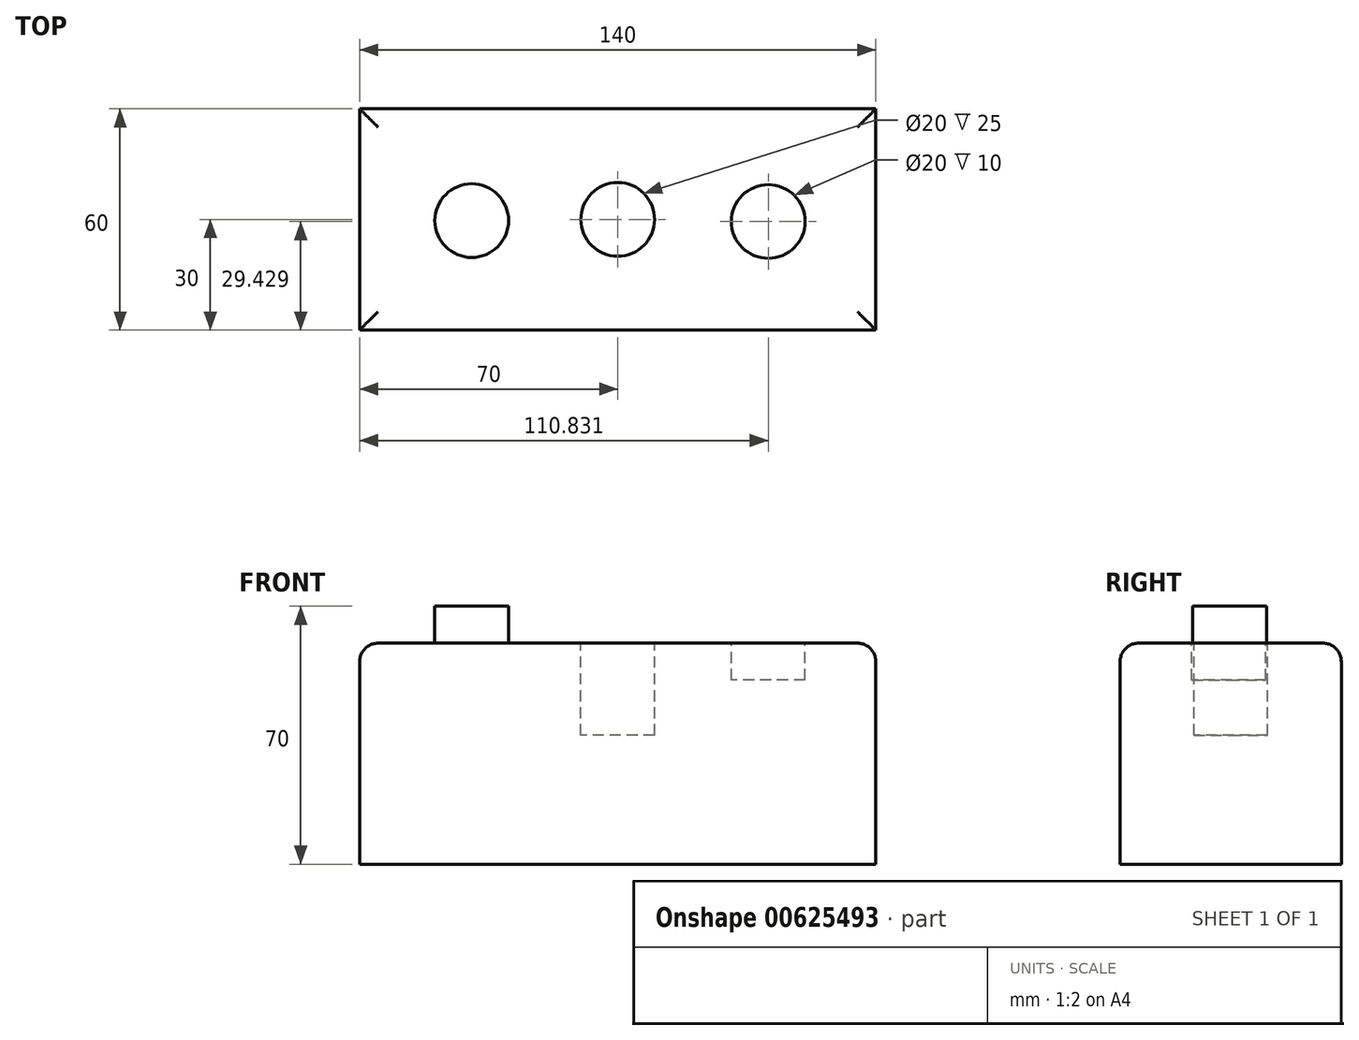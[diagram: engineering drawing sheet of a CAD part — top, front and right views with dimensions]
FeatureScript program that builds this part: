
annotation { "Feature Type Name" : "Feature", "Feature Type Description" : "" }
export const myFeature = defineFeature(function(context is Context, id is Id, definition is map)
    precondition{}
    {
        {
            var Q0;
            Q0=qCreatedBy(makeId("Top.planeOp"),FACE);
            var sketch = newSketch(context, id + "F0", { "sketchPlane" : qUnion([Q0])});
            skLineSegment(sketch, "E0.bottom", {"start": v(70, -30) * mm, "end": v(-70, -30) * mm});
            skLineSegment(sketch, "E0.top", {"start": v(70, 30) * mm, "end": v(-70, 30) * mm});
            skLineSegment(sketch, "E0.left", {"start": v(70, -30) * mm, "end": v(70, 30) * mm});
            skLineSegment(sketch, "E0.right", {"start": v(-70, -30) * mm, "end": v(-70, 30) * mm});
            skPoint(sketch, "E0.middle", {"position": v(0, 0) * mm});
            skSolve(sketch);
        }
        {
            var Q0;
            Q0 = qSketchRegion(id + "F0", true);
            extrude(context, id + "F1", {"entities" : qUnion([Q0]), "depth" : 60 * mm, "offsetDistance" : 25 * mm});
        }
        {
            var Q0;
            Q0=makeQuery(id+"F1.opExtrude","CAP_FACE",FACE,{"disambiguationData":[OSD([sQuery(id+"F0.wireOp",EDGE,"E0.bottom"),sQuery(id+"F0.wireOp",EDGE,"E0.top"),sQuery(id+"F0.wireOp",EDGE,"E0.left"),sQuery(id+"F0.wireOp",EDGE,"E0.right")])],"isStart":false});
            var sketch = newSketch(context, id + "F2", { "sketchPlane" : qUnion([Q0])});
            skLineSegment(sketch, "E1", {"start": v(-70, 0) * mm, "end": v(-50, 0) * mm});
            skSolve(sketch);
        }
        {
            var Q0;
            {var subQ1=makeQuery(id+"F1.opExtrude","CAP_EDGE",EDGE,{"disambiguationData":[OSD([sQuery(id+"F0.wireOp",EDGE,"E0.bottom")])],"isStart":false});Q0=makeQuery(id+"F2.imprint","IMPRINT",FACE,{"disambiguationData":[TD([[makeQuery(id+"F2.imprint","IMPRINT",EDGE,{"derivedFrom":subQ1}),-1.0]])]});}
            var sketch = newSketch(context, id + "F3", { "sketchPlane" : qUnion([Q0])});
            skCircle(sketch, "E2", {"center": v(-39.6, -0.32) * mm, "radius": 10 * mm});
            skPoint(sketch, "E2.first.point", {"position": v(-49.6, 0) * mm});
            skPoint(sketch, "E2.second.point", {"position": v(-29.6, 0) * mm});
            skPoint(sketch, "E2.third.point", {"position": v(-40.85, -10.24) * mm});
            skSolve(sketch);
        }
        {
            var Q0;
            {var subQ1=makeQuery(id+"F1.opExtrude","CAP_EDGE",EDGE,{"disambiguationData":[OSD([sQuery(id+"F0.wireOp",EDGE,"E0.bottom")])],"isStart":false});Q0=makeQuery(id+"F2.imprint","IMPRINT",FACE,{"disambiguationData":[TD([[makeQuery(id+"F2.imprint","IMPRINT",EDGE,{"derivedFrom":subQ1}),-1.0]])]});}
            var sketch = newSketch(context, id + "F4", { "sketchPlane" : qUnion([Q0])});
            skCircle(sketch, "E3", {"center": v(0, 0) * mm, "radius": 10 * mm});
            skSolve(sketch);
        }
        {
            var Q0;
            {var subQ1=makeQuery(id+"F1.opExtrude","CAP_EDGE",EDGE,{"disambiguationData":[OSD([sQuery(id+"F0.wireOp",EDGE,"E0.bottom")])],"isStart":false});Q0=makeQuery(id+"F2.imprint","IMPRINT",FACE,{"disambiguationData":[TD([[makeQuery(id+"F2.imprint","IMPRINT",EDGE,{"derivedFrom":subQ1}),-1.0]])]});}
            var sketch = newSketch(context, id + "F5", { "sketchPlane" : qUnion([Q0])});
            skCircle(sketch, "E4", {"center": v(40.83, -0.57) * mm, "radius": 10 * mm});
            skPoint(sketch, "E4.first.point", {"position": v(50.81, 0) * mm});
            skPoint(sketch, "E4.second.point", {"position": v(30.85, 0) * mm});
            skPoint(sketch, "E4.third.point", {"position": v(33.92, 6.66) * mm});
            skSolve(sketch);
        }
        {
            var Q0;
            Q0 = qSketchRegion(id + "F3", true);
            extrude(context, id + "F6", {"entities" : qUnion([Q0]), "operationType" : NewBodyOperationType.ADD, "depth" : 10 * mm, "offsetDistance" : 25 * mm});
        }
        {
            var Q0;
            Q0 = qSketchRegion(id + "F4", true);
            extrude(context, id + "F7", {"entities" : qUnion([Q0]), "operationType" : NewBodyOperationType.REMOVE, "oppositeDirection" : true, "depth" : 25 * mm, "offsetDistance" : 25 * mm});
        }
        {
            var Q0;
            Q0 = qSketchRegion(id + "F5", true);
            extrude(context, id + "F8", {"entities" : qUnion([Q0]), "operationType" : NewBodyOperationType.REMOVE, "oppositeDirection" : true, "depth" : 10 * mm, "offsetDistance" : 25 * mm});
        }
        {
            var Q0;
            Q0=makeQuery(id+"F1.opExtrude","CAP_EDGE",EDGE,{"disambiguationData":[OSD([sQuery(id+"F0.wireOp",EDGE,"E0.right")])],"isStart":false});
            var Q1;
            Q1=makeQuery(id+"F1.opExtrude","CAP_EDGE",EDGE,{"disambiguationData":[OSD([sQuery(id+"F0.wireOp",EDGE,"E0.left")])],"isStart":false});
            var Q2;
            Q2=makeQuery(id+"F1.opExtrude","CAP_EDGE",EDGE,{"disambiguationData":[OSD([sQuery(id+"F0.wireOp",EDGE,"E0.bottom")])],"isStart":false});
            var Q3;
            Q3=makeQuery(id+"F1.opExtrude","CAP_EDGE",EDGE,{"disambiguationData":[OSD([sQuery(id+"F0.wireOp",EDGE,"E0.top")])],"isStart":false});
            fillet(context, id + "F9", {"entities" : qUnion([Q0, Q1, Q2, Q3]), "radius" : 5 * mm, "tangentPropagation" : true, "allowEdgeOverflow" : false});
        }
    });
